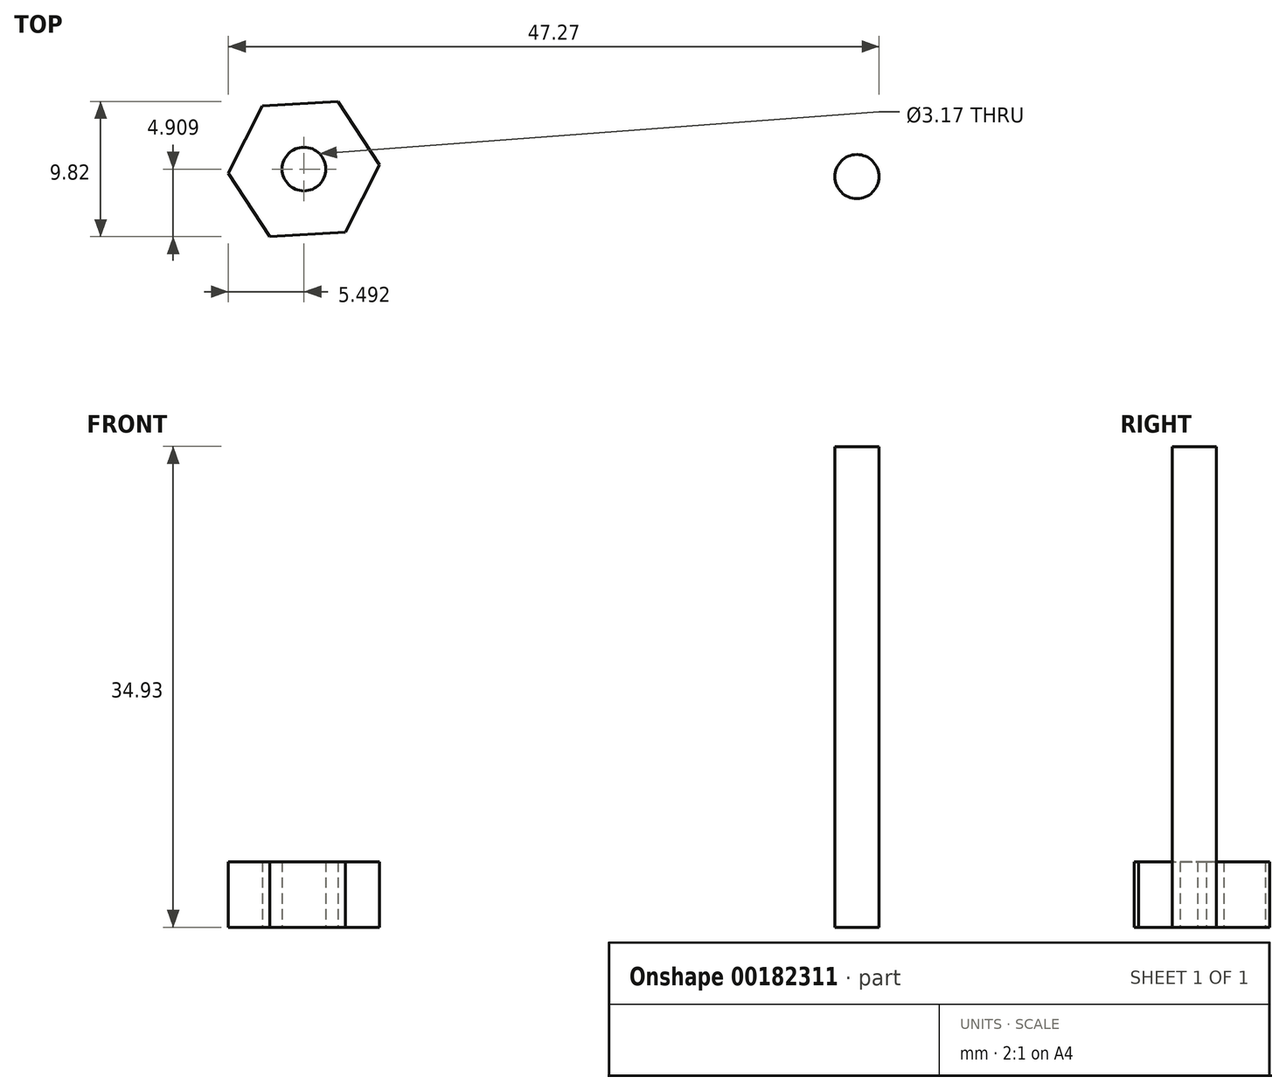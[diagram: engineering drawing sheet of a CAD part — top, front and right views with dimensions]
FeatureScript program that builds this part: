
annotation { "Feature Type Name" : "Feature", "Feature Type Description" : "" }
export const myFeature = defineFeature(function(context is Context, id is Id, definition is map)
    precondition{}
    {
        {
            var Q0;
            Q0=qCreatedBy(makeId("Top.planeOp"),FACE);
            var sketch = newSketch(context, id + "F0", { "sketchPlane" : qUnion([Q0])});
            skCircle(sketch, "E0.cCircle", {"center": v(-36, 10.53) * mm, "radius": 4.76 * mm, "construction": true});
            skLineSegment(sketch, "E0.0", {"start": v(-30.52, 10.84) * mm, "end": v(-33, 5.93) * mm});
            skLineSegment(sketch, "E0.1", {"start": v(-33, 5.93) * mm, "end": v(-38.49, 5.62) * mm});
            skLineSegment(sketch, "E0.2", {"start": v(-38.49, 5.62) * mm, "end": v(-41.5, 10.22) * mm});
            skLineSegment(sketch, "E0.3", {"start": v(-41.5, 10.22) * mm, "end": v(-39.02, 15.13) * mm});
            skLineSegment(sketch, "E0.4", {"start": v(-39.02, 15.13) * mm, "end": v(-33.53, 15.44) * mm});
            skLineSegment(sketch, "E0.5", {"start": v(-33.53, 15.44) * mm, "end": v(-30.52, 10.84) * mm});
            skPoint(sketch, "E0.0.midPoint", {"position": v(-31.76, 8.38) * mm});
            skCircle(sketch, "E1", {"center": v(-36, 10.53) * mm, "radius": 1.59 * mm});
            skSolve(sketch);
        }
        {
            var Q0;
            Q0 = qSketchRegion(id + "F0", true);
            extrude(context, id + "F1", {"entities" : qUnion([Q0]), "depth" : 4.76 * mm});
        }
        {
            var Q0;
            Q0=qCreatedBy(makeId("Top.planeOp"),FACE);
            var sketch = newSketch(context, id + "F2", { "sketchPlane" : qUnion([Q0])});
            skCircle(sketch, "E2", {"center": v(4.17, 9.98) * mm, "radius": 1.6 * mm});
            skSolve(sketch);
        }
        {
            var Q0;
            Q0 = qSketchRegion(id + "F2", true);
            extrude(context, id + "F3", {"entities" : qUnion([Q0]), "depth" : 34.92 * mm});
        }
    });
